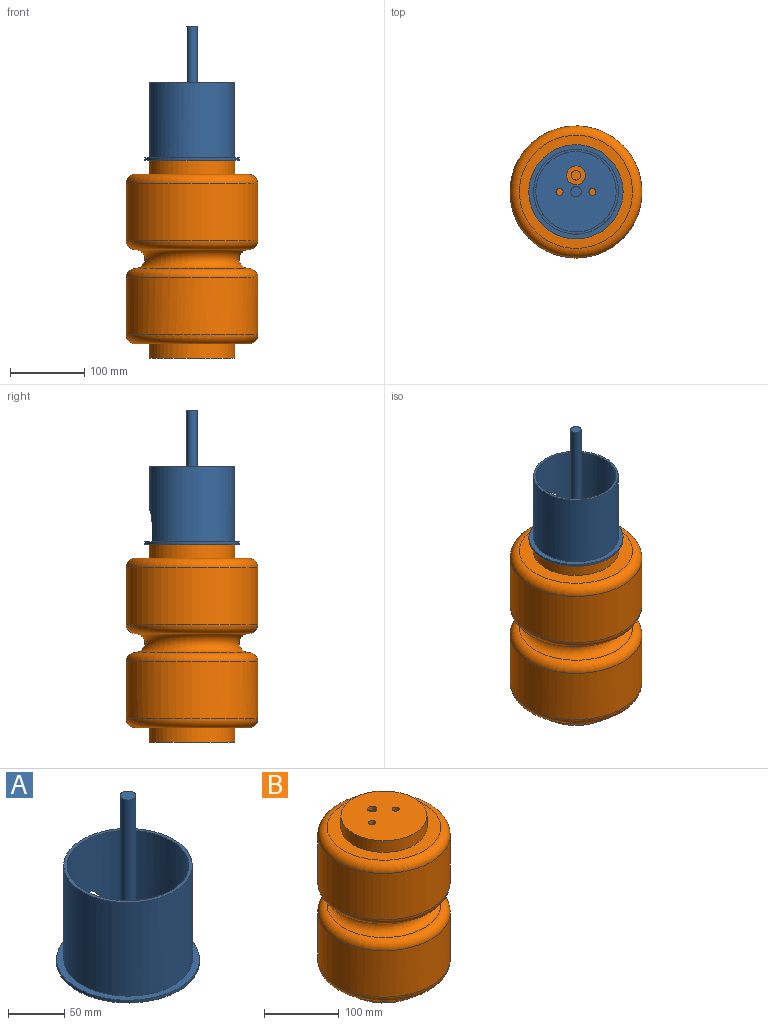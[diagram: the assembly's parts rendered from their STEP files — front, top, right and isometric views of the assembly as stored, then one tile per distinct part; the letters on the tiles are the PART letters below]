
ASSEMBLY  parts=2 mates=1
PART A: 14 faces, bbox 127x127x180.8 mm
  f0: cylinder r=4.76mm len=9.53mm, axis (0,0,-1), area 89.8mm2, adj f4,f5
  f1: cylinder r=4.76mm len=9.53mm, axis (0,0,-1), area 89.8mm2, adj f4,f5
  f2: cylinder r=12.7mm len=25.4mm, axis (0,0,-1), area 239.4mm2, adj f4,f5
  f3: cylinder r=63.5mm len=127mm, axis (0,0,-1), area 1196.9mm2, adj f4,f5
  f4: plane 127x127mm, normal (0,0,1), area 10932.2mm2, adj f0,f1,f2,f3,f6,f7,f9,f11
  f5: plane 127x127mm, normal (0,0,-1), area 12018.5mm2, adj f0,f1,f2,f3
  f6: cylinder r=54.15mm len=108.3mm, axis (0,0,-1), area 32999.6mm2, adj f4,f8,f9,f10,f11
  f7: cylinder r=57.15mm len=114.3mm, axis (0,0,-1), area 34918mm2, adj f4,f8,f9,f10,f11
  f8: plane 114.3x114.3mm, normal (0,0,1), area 1049mm2, adj f6,f7
  f9: plane 25.4x3.19mm, normal (-1,0,0), area 81.1mm2, adj f4,f6,f7,f10
  f10: cylinder r=19.05mm len=38.1mm, axis (0,-1,0), area 185.2mm2, adj f6,f7,f9,f11
  f11: plane 25.4x3.19mm, normal (1,0,0), area 81.1mm2, adj f4,f6,f7,f10
  f12: cylinder r=7mm len=177.8mm, axis (0,0,-1), area 7820.1mm2, adj f4,f13
  f13: plane 14x14mm, normal (0,0,1), area 153.9mm2, adj f12
PART B: 39 faces, bbox 194.2x194.2x266.7 mm
  f0: plane 102.87x102.87mm, normal (0,0,-1), area 7408.7mm2, adj f1,f13,f15,f19
  f1: cylinder r=51.44mm len=102.87mm, axis (0,0,-1), area 6156.5mm2, adj f0,f2
  f2: plane 152.4x152.4mm, normal (0,0,-1), area 9930.2mm2, adj f1,f11
  f3: cylinder r=82.55mm len=165.1mm, axis (0,0,-1), area 39523.2mm2, adj f4,f11
  f4: torus R=76.2mm, axis (0,0,-1), area 5029mm2, adj f3,f5
  f5: torus R=76.2mm, axis (0,0,-1), area 24093.3mm2, adj f4,f6
  f6: torus R=76.2mm, axis (0,0,-1), area 5029mm2, adj f5,f7
  f7: cylinder r=82.55mm len=165.1mm, axis (0,0,-1), area 39523.2mm2, adj f6,f12
  f8: plane 152.4x152.4mm, normal (0,0,1), area 9930.2mm2, adj f9,f12
  f9: cylinder r=51.44mm len=102.87mm, axis (0,0,-1), area 6156.5mm2, adj f8,f10
  f10: plane 102.87x102.87mm, normal (0,0,1), area 7923.3mm2, adj f9,f17
  f11: torus R=76.2mm, axis (0,0,-1), area 5029mm2, adj f2,f3
  f12: torus R=76.2mm, axis (0,0,1), area 5029mm2, adj f7,f8
  f13: cylinder r=11.11mm len=22.23mm, axis (0,0,1), area 1117.3mm2, adj f0,f14
  f14: plane 22.23x22.23mm, normal (0,0,-1), area 387.9mm2, adj f13
  f15: cylinder r=11.11mm len=22.23mm, axis (0,0,1), area 1117.3mm2, adj f0,f16
  f16: plane 22.23x22.23mm, normal (0,0,-1), area 387.9mm2, adj f15
  f17: cylinder r=11.11mm len=22.23mm, axis (0,0,-1), area 1117.3mm2, adj f10,f18
  f18: plane 22.23x22.23mm, normal (0,0,1), area 387.9mm2, adj f17
  f19: cylinder r=6.35mm len=12.7mm, axis (0,0,1), area 253.4mm2, adj f0,f20
  f20: plane 115.57x115.57mm, normal (0,0,1), area 10220.9mm2, adj f19,f21,f33,f35
  f21: cylinder r=57.79mm len=115.57mm, axis (0,0,-1), area 6916.6mm2, adj f20,f22
  f22: plane 152.4x152.4mm, normal (0,0,1), area 7751.4mm2, adj f21,f31
  f23: cylinder r=88.9mm len=177.8mm, axis (0,0,-1), area 42563.4mm2, adj f24,f31
  f24: torus R=76.2mm, axis (0,0,-1), area 10564.6mm2, adj f23,f25
  f25: torus R=76.2mm, axis (0,0,-1), area 17075.6mm2, adj f24,f26
  f26: torus R=76.2mm, axis (0,0,-1), area 10564.6mm2, adj f25,f27
  f27: cylinder r=88.9mm len=177.8mm, axis (0,0,-1), area 42563.4mm2, adj f26,f32
  f28: plane 152.4x152.4mm, normal (0,0,-1), area 7751.4mm2, adj f29,f32
  f29: cylinder r=57.79mm len=115.57mm, axis (0,0,-1), area 6916.6mm2, adj f28,f30
  f30: plane 115.57x115.57mm, normal (0,0,-1), area 10418.9mm2, adj f29,f37
  f31: torus R=76.2mm, axis (0,0,-1), area 10564.6mm2, adj f22,f23
  f32: torus R=76.2mm, axis (0,0,1), area 10564.6mm2, adj f27,f28
  f33: cylinder r=4.76mm len=16mm, axis (0,0,1), area 478.8mm2, adj f20,f34
  f34: plane 9.53x9.53mm, normal (0,0,1), area 71.3mm2, adj f33
  f35: cylinder r=4.76mm len=16mm, axis (0,0,1), area 478.8mm2, adj f20,f36
  f36: plane 9.53x9.53mm, normal (0,0,1), area 71.3mm2, adj f35
  f37: cylinder r=4.76mm len=16mm, axis (0,0,-1), area 478.8mm2, adj f30,f38
  f38: plane 9.53x9.53mm, normal (0,0,-1), area 71.3mm2, adj f37
PLACE A t=(-56.8,70.44,153.35)mm
PLACE B t=(-56.8,70.44,20)mm
MATE fastened B.f1 <-> A.f3  axis (0,0,1) through (-56.8,70.44,153.35)mm
